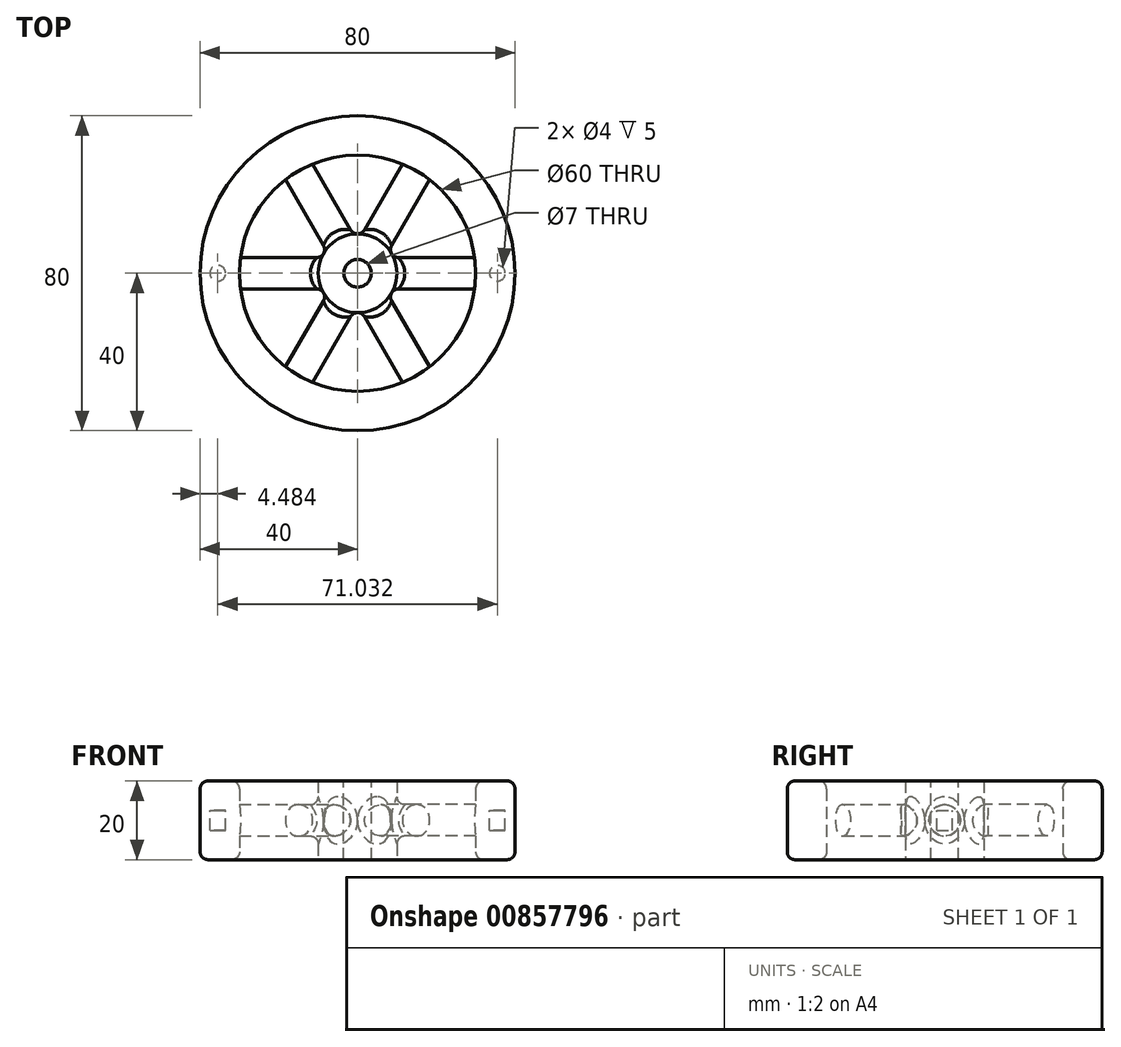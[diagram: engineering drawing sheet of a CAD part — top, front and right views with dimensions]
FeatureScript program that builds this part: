
annotation { "Feature Type Name" : "Feature", "Feature Type Description" : "" }
export const myFeature = defineFeature(function(context is Context, id is Id, definition is map)
    precondition{}
    {
        {
            var Q0;
            Q0=qCreatedBy(makeId("Top.planeOp"),FACE);
            var sketch = newSketch(context, id + "F0", { "sketchPlane" : qUnion([Q0])});
            skCircle(sketch, "E0", {"center": v(0, 0) * mm, "radius": 40 * mm});
            skCircle(sketch, "E1", {"center": v(0, 0) * mm, "radius": 30 * mm});
            skCircle(sketch, "E2", {"center": v(0, 0) * mm, "radius": 10 * mm});
            skSolve(sketch);
        }
        {
            var Q0;
            Q0=makeQuery(id+"F0.imprint","IMPRINT",FACE,{"disambiguationData":[TD([[makeQuery(id+"F0.imprint","IMPRINT",EDGE,{"derivedFrom":sQuery(id+"F0.wireOp",EDGE,"E0")}),1.0]])]});
            var Q1;
            Q1=makeQuery(id+"F0.imprint","IMPRINT",FACE,{"disambiguationData":[TD([[makeQuery(id+"F0.imprint","IMPRINT",EDGE,{"derivedFrom":sQuery(id+"F0.wireOp",EDGE,"E2")}),1.0]])]});
            extrude(context, id + "F1", {"entities" : qUnion([Q0, Q1]), "depth" : 20 * mm, "offsetDistance" : 25 * mm});
        }
        {
            var Q0;
            Q0=qCreatedBy(makeId("Right.planeOp"),FACE);
            var sketch = newSketch(context, id + "F2", { "sketchPlane" : qUnion([Q0])});
            skLineSegment(sketch, "E3", {"start": v(0, 0) * mm, "end": v(0, 10) * mm, "construction": true});
            skCircle(sketch, "E4", {"center": v(0, 10) * mm, "radius": 4 * mm});
            skSolve(sketch);
        }
        {
            var Q0;
            Q0 = qSketchRegion(id + "F2", true);
            var Q1;
            Q1=makeQuery(id+"F1.opExtrude","SWEPT_FACE",FACE,{"disambiguationData":[OSD([sQuery(id+"F0.wireOp",EDGE,"E1")])]});
            extrude(context, id + "F3", {"entities" : qUnion([Q0]), "endBound" : BoundingType.UP_TO_SURFACE, "depth" : 35 * mm, "endBoundEntityFace" : qUnion([Q1]), "offsetDistance" : 25 * mm});
        }
        {
            var Q0;
            Q0=qCreatedBy(makeId("Right.planeOp"),FACE);
            var sketch = newSketch(context, id + "F4", { "sketchPlane" : qUnion([Q0])});
            skLineSegment(sketch, "E5", {"start": v(0, -36.73) * mm, "end": v(0, 44.04) * mm, "construction": true});
            skSolve(sketch);
        }
        {
            var Q0;
            Q0=makeQuery(id+"F3.opExtrude","SWEPT_BODY",BODY,{"disambiguationData":[OSD([sQuery(id+"F2.wireOp",EDGE,"E4")])]});
            var Q1;
            Q1=sQuery(id+"F4.wireOp",EDGE,"E5");
            circularPattern(context, id + "F5", {"entities" : qUnion([Q0]), "axis" : qUnion([Q1]), "angle" : 360 * degree, "instanceCount" : 6, "equalSpace" : true});
        }
        {
            var Q0;
            Q0=makeQuery(id+"F1.opExtrude","CAP_EDGE",EDGE,{"disambiguationData":[OSD([sQuery(id+"F0.wireOp",EDGE,"E0")])],"isStart":false});
            var Q1;
            Q1=makeQuery(id+"F1.opExtrude","CAP_EDGE",EDGE,{"disambiguationData":[OSD([sQuery(id+"F0.wireOp",EDGE,"E1")])],"isStart":false});
            var Q2;
            Q2=makeQuery(id+"F1.opExtrude","CAP_EDGE",EDGE,{"disambiguationData":[OSD([sQuery(id+"F0.wireOp",EDGE,"E0")])],"isStart":true});
            var Q3;
            Q3=makeQuery(id+"F1.opExtrude","CAP_EDGE",EDGE,{"disambiguationData":[OSD([sQuery(id+"F0.wireOp",EDGE,"E1")])],"isStart":true});
            fillet(context, id + "F6", {"entities" : qUnion([Q0, Q1, Q2, Q3]), "radius" : 2 * mm, "tangentPropagation" : true, "allowEdgeOverflow" : false});
        }
        {
            var Q0;
            Q0=makeQuery(id+"F3.opExtrude","SWEPT_BODY",BODY,{"disambiguationData":[OSD([sQuery(id+"F2.wireOp",EDGE,"E4")])]});
            var Q1;
            Q1=makeQuery(id+"F5.opPattern","COPY",BODY,{"derivedFrom":makeQuery(id+"F3.opExtrude","SWEPT_BODY",BODY,{"disambiguationData":[OSD([sQuery(id+"F2.wireOp",EDGE,"E4")])]}),"instanceName":"5"});
            var Q2;
            Q2=makeQuery(id+"F5.opPattern","COPY",BODY,{"derivedFrom":makeQuery(id+"F3.opExtrude","SWEPT_BODY",BODY,{"disambiguationData":[OSD([sQuery(id+"F2.wireOp",EDGE,"E4")])]}),"instanceName":"4"});
            var Q3;
            Q3=makeQuery(id+"F5.opPattern","COPY",BODY,{"derivedFrom":makeQuery(id+"F3.opExtrude","SWEPT_BODY",BODY,{"disambiguationData":[OSD([sQuery(id+"F2.wireOp",EDGE,"E4")])]}),"instanceName":"3"});
            var Q4;
            Q4=makeQuery(id+"F5.opPattern","COPY",BODY,{"derivedFrom":makeQuery(id+"F3.opExtrude","SWEPT_BODY",BODY,{"disambiguationData":[OSD([sQuery(id+"F2.wireOp",EDGE,"E4")])]}),"instanceName":"2"});
            var Q5;
            Q5=makeQuery(id+"F1.opExtrude","SWEPT_BODY",BODY,{"disambiguationData":[OSD([sQuery(id+"F0.wireOp",EDGE,"E0"),sQuery(id+"F0.wireOp",EDGE,"E1")])]});
            var Q6;
            Q6=makeQuery(id+"F1.opExtrude","SWEPT_BODY",BODY,{"disambiguationData":[OSD([sQuery(id+"F0.wireOp",EDGE,"E2")])]});
            var Q7;
            Q7=makeQuery(id+"F5.opPattern","COPY",BODY,{"derivedFrom":makeQuery(id+"F3.opExtrude","SWEPT_BODY",BODY,{"disambiguationData":[OSD([sQuery(id+"F2.wireOp",EDGE,"E4")])]}),"instanceName":"1"});
            booleanBodies(context, id + "F7", {"operationType" : BooleanOperationType.UNION, "tools" : qUnion([Q0, Q1, Q2, Q3, Q4, Q5, Q6, Q7])});
        }
        {
            var Q0;
            Q0=makeQuery(id+"F5.opPattern","COPY",EDGE,{"derivedFrom":makeQuery(id+"F3.opExtrude","TWEAK_EDGE",EDGE,{"derivedFrom":[makeQuery(id+"F1.opExtrude","SWEPT_FACE",FACE,{"disambiguationData":[OSD([sQuery(id+"F0.wireOp",EDGE,"E1")])]}),makeQuery(id+"F2.imprint","IMPRINT",EDGE,{"derivedFrom":sQuery(id+"F2.wireOp",EDGE,"E4")})]}),"instanceName":"1"});
            var Q1;
            Q1=makeQuery(id+"F3.opExtrude","TWEAK_EDGE",EDGE,{"derivedFrom":[makeQuery(id+"F1.opExtrude","SWEPT_FACE",FACE,{"disambiguationData":[OSD([sQuery(id+"F0.wireOp",EDGE,"E1")])]}),makeQuery(id+"F2.imprint","IMPRINT",EDGE,{"derivedFrom":sQuery(id+"F2.wireOp",EDGE,"E4")})]});
            var Q2;
            Q2=makeQuery(id+"F5.opPattern","COPY",EDGE,{"derivedFrom":makeQuery(id+"F3.opExtrude","TWEAK_EDGE",EDGE,{"derivedFrom":[makeQuery(id+"F1.opExtrude","SWEPT_FACE",FACE,{"disambiguationData":[OSD([sQuery(id+"F0.wireOp",EDGE,"E1")])]}),makeQuery(id+"F2.imprint","IMPRINT",EDGE,{"derivedFrom":sQuery(id+"F2.wireOp",EDGE,"E4")})]}),"instanceName":"2"});
            var Q3;
            Q3=makeQuery(id+"F5.opPattern","COPY",EDGE,{"derivedFrom":makeQuery(id+"F3.opExtrude","TWEAK_EDGE",EDGE,{"derivedFrom":[makeQuery(id+"F1.opExtrude","SWEPT_FACE",FACE,{"disambiguationData":[OSD([sQuery(id+"F0.wireOp",EDGE,"E1")])]}),makeQuery(id+"F2.imprint","IMPRINT",EDGE,{"derivedFrom":sQuery(id+"F2.wireOp",EDGE,"E4")})]}),"instanceName":"3"});
            var Q4;
            Q4=makeQuery(id+"F5.opPattern","COPY",EDGE,{"derivedFrom":makeQuery(id+"F3.opExtrude","TWEAK_EDGE",EDGE,{"derivedFrom":[makeQuery(id+"F1.opExtrude","SWEPT_FACE",FACE,{"disambiguationData":[OSD([sQuery(id+"F0.wireOp",EDGE,"E1")])]}),makeQuery(id+"F2.imprint","IMPRINT",EDGE,{"derivedFrom":sQuery(id+"F2.wireOp",EDGE,"E4")})]}),"instanceName":"4"});
            var Q5;
            Q5=makeQuery(id+"F5.opPattern","COPY",EDGE,{"derivedFrom":makeQuery(id+"F3.opExtrude","TWEAK_EDGE",EDGE,{"derivedFrom":[makeQuery(id+"F1.opExtrude","SWEPT_FACE",FACE,{"disambiguationData":[OSD([sQuery(id+"F0.wireOp",EDGE,"E1")])]}),makeQuery(id+"F2.imprint","IMPRINT",EDGE,{"derivedFrom":sQuery(id+"F2.wireOp",EDGE,"E4")})]}),"instanceName":"5"});
            var Q6;
            Q6=makeQuery(id+"F7.opBoolean","INTERSECT",EDGE,{"derivedFrom":[makeQuery(id+"F1.opExtrude","SWEPT_FACE",FACE,{"disambiguationData":[OSD([sQuery(id+"F0.wireOp",EDGE,"E2")])]}),makeQuery(id+"F5.opPattern","COPY",FACE,{"derivedFrom":makeQuery(id+"F3.opExtrude","SWEPT_FACE",FACE,{"disambiguationData":[OSD([sQuery(id+"F2.wireOp",EDGE,"E4")])]}),"instanceName":"2"})]});
            var Q7;
            Q7=makeQuery(id+"F7.opBoolean","INTERSECT",EDGE,{"derivedFrom":[makeQuery(id+"F1.opExtrude","SWEPT_FACE",FACE,{"disambiguationData":[OSD([sQuery(id+"F0.wireOp",EDGE,"E2")])]}),makeQuery(id+"F5.opPattern","COPY",FACE,{"derivedFrom":makeQuery(id+"F3.opExtrude","SWEPT_FACE",FACE,{"disambiguationData":[OSD([sQuery(id+"F2.wireOp",EDGE,"E4")])]}),"instanceName":"1"})]});
            var Q8;
            Q8=makeQuery(id+"F7.opBoolean","INTERSECT",EDGE,{"derivedFrom":[makeQuery(id+"F1.opExtrude","SWEPT_FACE",FACE,{"disambiguationData":[OSD([sQuery(id+"F0.wireOp",EDGE,"E2")])]}),makeQuery(id+"F5.opPattern","COPY",FACE,{"derivedFrom":makeQuery(id+"F3.opExtrude","SWEPT_FACE",FACE,{"disambiguationData":[OSD([sQuery(id+"F2.wireOp",EDGE,"E4")])]}),"instanceName":"3"})]});
            var Q9;
            Q9=makeQuery(id+"F7.opBoolean","INTERSECT",EDGE,{"derivedFrom":[makeQuery(id+"F1.opExtrude","SWEPT_FACE",FACE,{"disambiguationData":[OSD([sQuery(id+"F0.wireOp",EDGE,"E2")])]}),makeQuery(id+"F5.opPattern","COPY",FACE,{"derivedFrom":makeQuery(id+"F3.opExtrude","SWEPT_FACE",FACE,{"disambiguationData":[OSD([sQuery(id+"F2.wireOp",EDGE,"E4")])]}),"instanceName":"4"})]});
            var Q10;
            Q10=makeQuery(id+"F7.opBoolean","INTERSECT",EDGE,{"derivedFrom":[makeQuery(id+"F1.opExtrude","SWEPT_FACE",FACE,{"disambiguationData":[OSD([sQuery(id+"F0.wireOp",EDGE,"E2")])]}),makeQuery(id+"F3.opExtrude","SWEPT_FACE",FACE,{"disambiguationData":[OSD([sQuery(id+"F2.wireOp",EDGE,"E4")])]})]});
            var Q11;
            Q11=makeQuery(id+"F7.opBoolean","INTERSECT",EDGE,{"derivedFrom":[makeQuery(id+"F1.opExtrude","SWEPT_FACE",FACE,{"disambiguationData":[OSD([sQuery(id+"F0.wireOp",EDGE,"E2")])]}),makeQuery(id+"F5.opPattern","COPY",FACE,{"derivedFrom":makeQuery(id+"F3.opExtrude","SWEPT_FACE",FACE,{"disambiguationData":[OSD([sQuery(id+"F2.wireOp",EDGE,"E4")])]}),"instanceName":"5"})]});
            fillet(context, id + "F8", {"entities" : qUnion([Q0, Q1, Q2, Q3, Q4, Q5, Q6, Q7, Q8, Q9, Q10, Q11]), "radius" : 2 * mm, "tangentPropagation" : true, "allowEdgeOverflow" : false});
        }
        {
            var Q0;
            Q0=makeQuery(id+"F1.opExtrude","CAP_FACE",FACE,{"disambiguationData":[OSD([sQuery(id+"F0.wireOp",EDGE,"E2")])],"isStart":false});
            var sketch = newSketch(context, id + "F9", { "sketchPlane" : qUnion([Q0])});
            skCircle(sketch, "E6", {"center": v(0, 0) * mm, "radius": 3.5 * mm});
            skSolve(sketch);
        }
        {
            var Q0;
            Q0 = qSketchRegion(id + "F9", true);
            extrude(context, id + "F10", {"entities" : qUnion([Q0]), "operationType" : NewBodyOperationType.REMOVE, "endBound" : BoundingType.THROUGH_ALL, "oppositeDirection" : true, "depth" : 25 * mm, "offsetDistance" : 25 * mm});
        }
        {
            var Q0;
            Q0=qCreatedBy(makeId("Front.planeOp"),FACE);
            var sketch = newSketch(context, id + "F11", { "sketchPlane" : qUnion([Q0])});
            skLineSegment(sketch, "E7", {"start": v(0, 0) * mm, "end": v(0, 10) * mm});
            skLineSegment(sketch, "E8", {"start": v(-10.33, 10) * mm, "end": v(11.36, 10) * mm});
            skSolve(sketch);
        }
        {
            var Q0;
            Q0=sQuery(id+"F11.wireOp",EDGE,"E8");
            cPlane(context, id + "F12", {"entities" : qUnion([Q0]), "cplaneType" : CPlaneType.LINE_ANGLE, "offset" : 25 * mm, "angle" : 90 * degree, "width" : 150 * mm, "height" : 150 * mm});
        }
        {
            var Q0;
            Q0=qCreatedBy(id+"F12.planeOp",FACE);
            var sketch = newSketch(context, id + "F13", { "sketchPlane" : qUnion([Q0])});
            skCircle(sketch, "E9", {"center": v(35.52, 0) * mm, "radius": 2 * mm});
            skCircle(sketch, "E10.MirrorC", {"center": v(-35.52, 0) * mm, "radius": 2 * mm});
            skSolve(sketch);
        }
        {
            var Q0;
            Q0 = qSketchRegion(id + "F13", true);
            extrude(context, id + "F14", {"entities" : qUnion([Q0]), "operationType" : NewBodyOperationType.REMOVE, "endBound" : BoundingType.SYMMETRIC, "oppositeDirection" : true, "depth" : 5 * mm, "offsetDistance" : 25 * mm});
        }
    });
